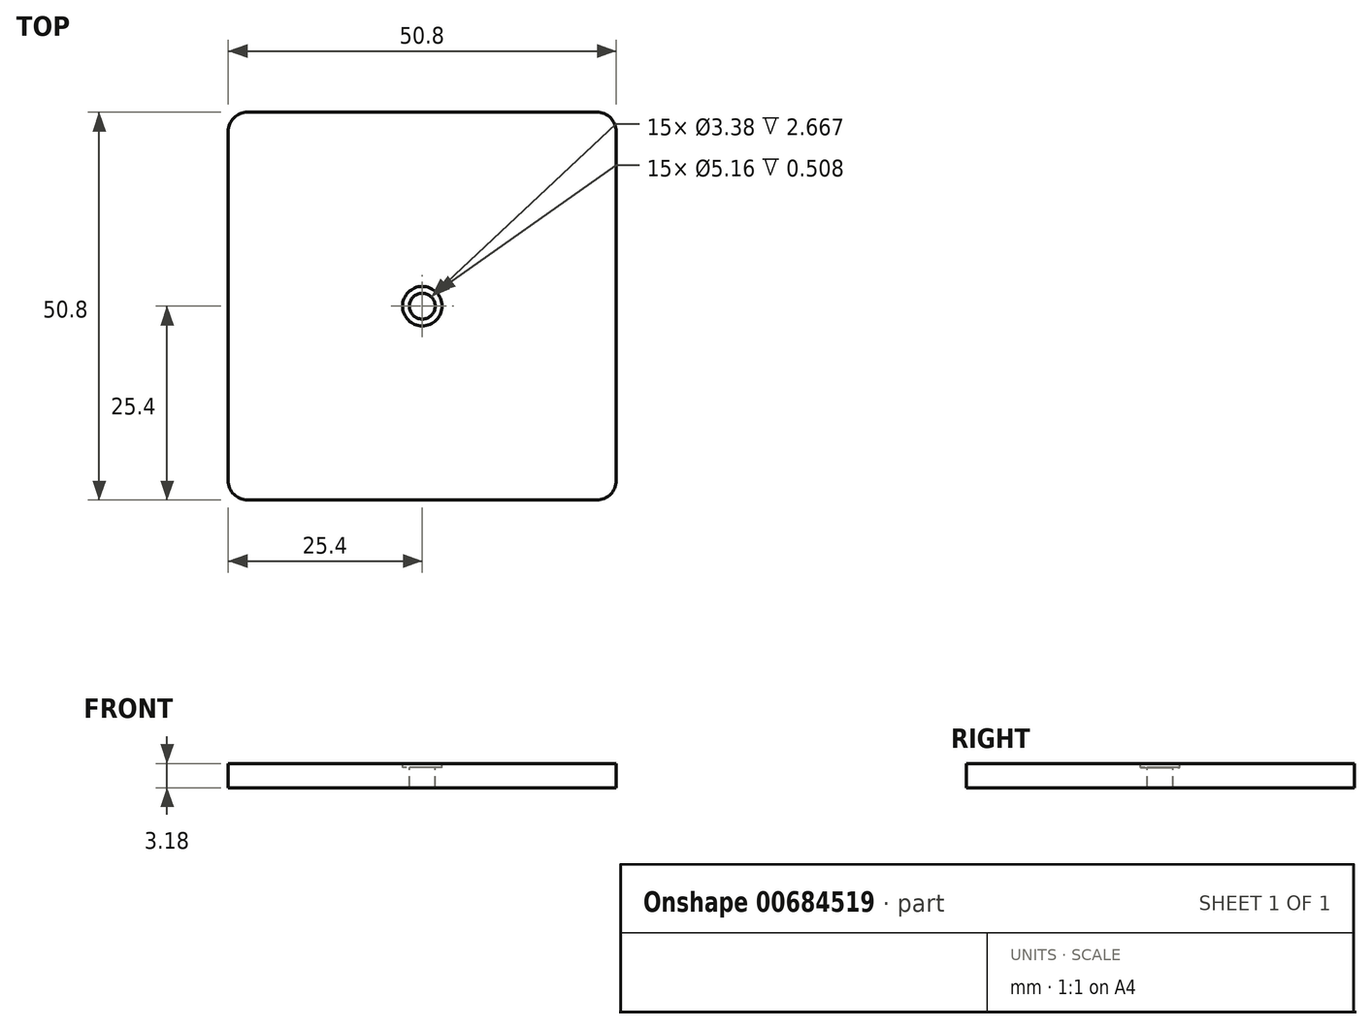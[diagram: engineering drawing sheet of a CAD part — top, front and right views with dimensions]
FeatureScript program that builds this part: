
annotation { "Feature Type Name" : "Feature", "Feature Type Description" : "" }
export const myFeature = defineFeature(function(context is Context, id is Id, definition is map)
    precondition{}
    {
        {
            var Q0;
            Q0=qCreatedBy(makeId("Top.planeOp"),FACE);
            var sketch = newSketch(context, id + "F0", { "sketchPlane" : qUnion([Q0])});
            skLineSegment(sketch, "E0.bottom", {"start": v(-25.4, -25.4) * mm, "end": v(25.4, -25.4) * mm});
            skLineSegment(sketch, "E0.top", {"start": v(-25.4, 25.4) * mm, "end": v(25.4, 25.4) * mm});
            skLineSegment(sketch, "E0.left", {"start": v(-25.4, -25.4) * mm, "end": v(-25.4, 25.4) * mm});
            skLineSegment(sketch, "E0.right", {"start": v(25.4, -25.4) * mm, "end": v(25.4, 25.4) * mm});
            skLineSegment(sketch, "E1", {"start": v(-25.4, -25.4) * mm, "end": v(25.4, 25.4) * mm, "construction": true});
            skCircle(sketch, "E2", {"center": v(0, 0) * mm, "radius": 2.58 * mm, "construction": true});
            skCircle(sketch, "E3", {"center": v(0, 0) * mm, "radius": 1.69 * mm, "construction": true});
            skCircle(sketch, "E4", {"center": v(0, 0) * mm, "radius": 2.45 * mm, "construction": true});
            skSolve(sketch);
        }
        {
            var Q0;
            Q0 = qSketchRegion(id + "F0", true);
            extrude(context, id + "F1", {"entities" : qUnion([Q0]), "endBound" : BoundingType.SYMMETRIC, "depth" : 3.17 * mm, "offsetDistance" : 25.4 * mm});
        }
        {
            var Q0;
            Q0=qCreatedBy(makeId("Front.planeOp"),FACE);
            var sketch = newSketch(context, id + "F2", { "sketchPlane" : qUnion([Q0])});
            skLineSegment(sketch, "E5", {"start": v(0, 1.59) * mm, "end": v(0, -1.59) * mm});
            skLineSegment(sketch, "E6", {"start": v(0, -1.59) * mm, "end": v(1.69, -1.59) * mm});
            skLineSegment(sketch, "E7", {"start": v(1.69, -1.59) * mm, "end": v(1.69, 1.08) * mm});
            skLineSegment(sketch, "E8", {"start": v(1.69, 1.08) * mm, "end": v(2.58, 1.08) * mm});
            skLineSegment(sketch, "E9", {"start": v(2.58, 1.08) * mm, "end": v(2.58, 1.59) * mm});
            skLineSegment(sketch, "E10", {"start": v(2.58, 1.59) * mm, "end": v(0, 1.59) * mm});
            skLineSegment(sketch, "E11", {"start": v(0, 1.59) * mm, "end": v(0, 4.76) * mm, "construction": true});
            skLineSegment(sketch, "E12", {"start": v(2.58, 1.08) * mm, "end": v(2.58, 0) * mm, "construction": true});
            skPoint(sketch, "E13", {"position": v(1.69, 0) * mm});
            skSolve(sketch);
        }
        {
            var Q0;
            Q0=makeQuery(id+"F2.imprint","IMPRINT",FACE,{"disambiguationData":[TD([[makeQuery(id+"F2.imprint","IMPRINT",EDGE,{"derivedFrom":sQuery(id+"F2.wireOp",EDGE,"E5")}),1.0]])]});
            var Q1;
            Q1=sQuery(id+"F2.wireOp",EDGE,"E11");
            revolve(context, id + "F3", {"operationType" : NewBodyOperationType.REMOVE, "entities" : qUnion([Q0]), "axis" : qUnion([Q1]), "revolveType" : RevolveType.FULL, "oppositeDirection" : true});
        }
        {
            var Q0;
            Q0=makeQuery(id+"F1.opExtrude","SWEPT_EDGE",EDGE,{"disambiguationData":[OSD([sQuery(id+"F0.wireOp",EDGE,"E0.bottom"),sQuery(id+"F0.wireOp",EDGE,"E0.left")])]});
            var Q1;
            Q1=makeQuery(id+"F1.opExtrude","SWEPT_EDGE",EDGE,{"disambiguationData":[OSD([sQuery(id+"F0.wireOp",EDGE,"E0.bottom"),sQuery(id+"F0.wireOp",EDGE,"E0.right")])]});
            var Q2;
            Q2=makeQuery(id+"F1.opExtrude","SWEPT_EDGE",EDGE,{"disambiguationData":[OSD([sQuery(id+"F0.wireOp",EDGE,"E0.top"),sQuery(id+"F0.wireOp",EDGE,"E0.right")])]});
            var Q3;
            Q3=makeQuery(id+"F1.opExtrude","SWEPT_EDGE",EDGE,{"disambiguationData":[OSD([sQuery(id+"F0.wireOp",EDGE,"E0.top"),sQuery(id+"F0.wireOp",EDGE,"E0.left")])]});
            fillet(context, id + "F4", {"entities" : qUnion([Q0, Q1, Q2, Q3]), "radius" : 2.54 * mm, "tangentPropagation" : true, "allowEdgeOverflow" : false});
        }
    });
